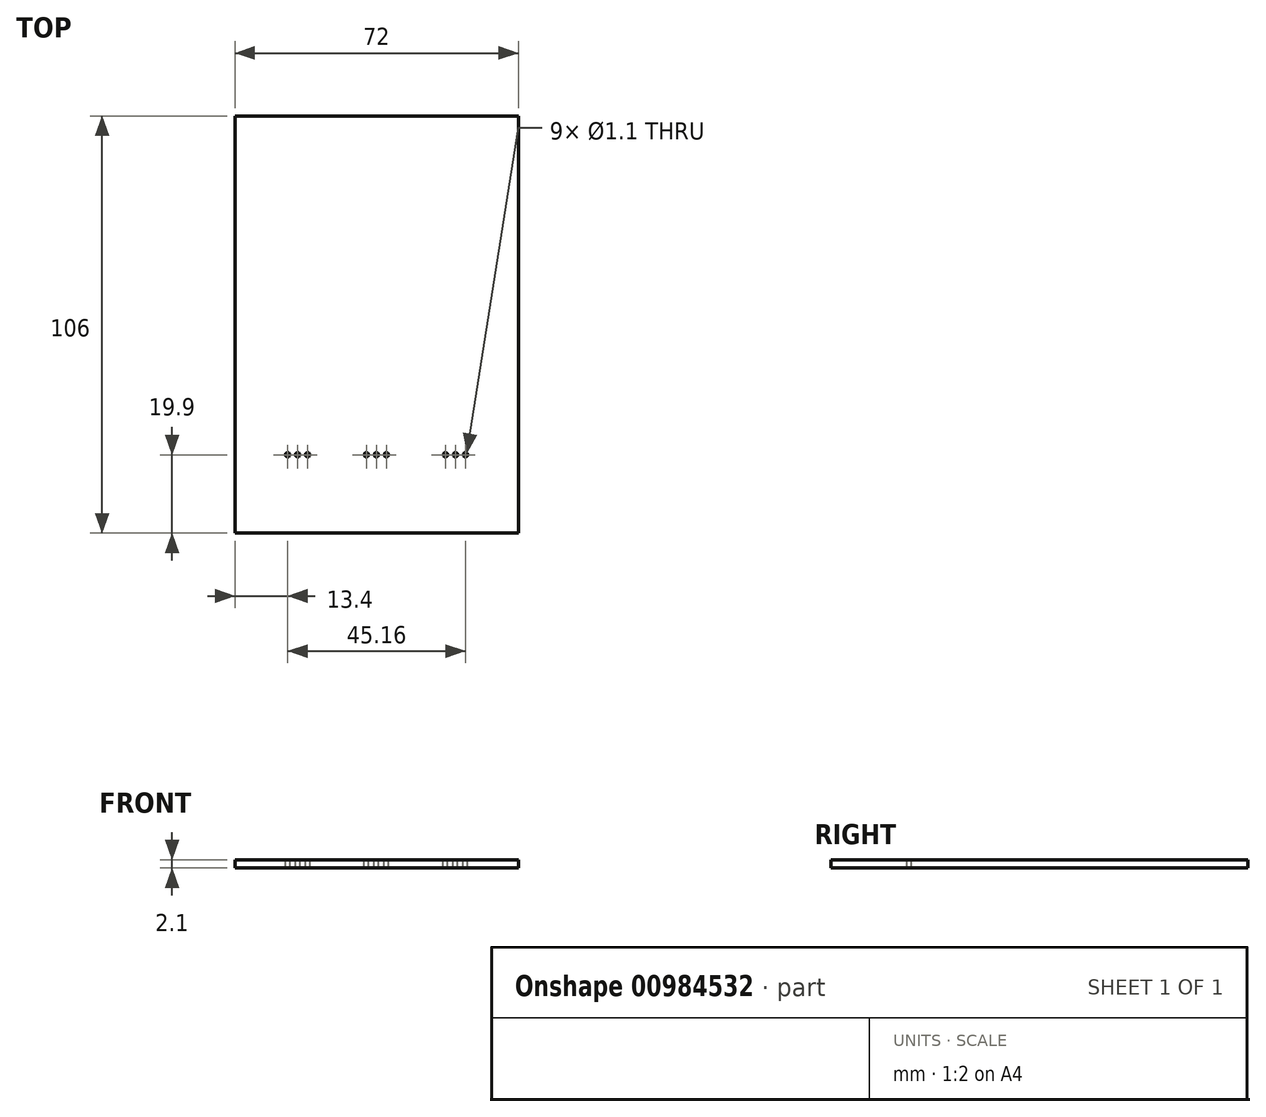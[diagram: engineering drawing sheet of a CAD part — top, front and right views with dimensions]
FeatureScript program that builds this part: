
annotation { "Feature Type Name" : "Feature", "Feature Type Description" : "" }
export const myFeature = defineFeature(function(context is Context, id is Id, definition is map)
    precondition{}
    {
        {
            var Q0;
            Q0=qCreatedBy(makeId("Top.planeOp"),FACE);
            var sketch = newSketch(context, id + "F0", { "sketchPlane" : qUnion([Q0])});
            skLineSegment(sketch, "E0.bottom", {"start": v(0, 0) * mm, "end": v(72, 0) * mm});
            skLineSegment(sketch, "E0.top", {"start": v(0, 106) * mm, "end": v(72, 106) * mm});
            skLineSegment(sketch, "E0.left", {"start": v(0, 0) * mm, "end": v(0, 106) * mm});
            skLineSegment(sketch, "E0.right", {"start": v(72, 0) * mm, "end": v(72, 106) * mm});
            skSolve(sketch);
        }
        {
            var Q0;
            Q0=makeQuery(id+"F0.imprint","IMPRINT",FACE,{"disambiguationData":[TD([[makeQuery(id+"F0.imprint","IMPRINT",EDGE,{"derivedFrom":sQuery(id+"F0.wireOp",EDGE,"E0.bottom")}),1.0]])]});
            extrude(context, id + "F1", {"entities" : qUnion([Q0]), "depth" : 2.1 * mm, "offsetDistance" : 25 * mm});
        }
        {
            var Q0;
            Q0=makeQuery(id+"F1.opExtrude","CAP_FACE",FACE,{"disambiguationData":[OSD([sQuery(id+"F0.wireOp",EDGE,"E0.bottom"),sQuery(id+"F0.wireOp",EDGE,"E0.top"),sQuery(id+"F0.wireOp",EDGE,"E0.left"),sQuery(id+"F0.wireOp",EDGE,"E0.right")])],"isStart":false});
            var sketch = newSketch(context, id + "F2", { "sketchPlane" : qUnion([Q0])});
            skPoint(sketch, "E1", {"position": v(13.4, 19.9) * mm});
            skPoint(sketch, "E2", {"position": v(15.94, 19.9) * mm});
            skPoint(sketch, "E3", {"position": v(18.48, 19.9) * mm});
            skPoint(sketch, "E4", {"position": v(33.4, 19.9) * mm});
            skPoint(sketch, "E5", {"position": v(35.94, 19.9) * mm});
            skPoint(sketch, "E6", {"position": v(38.48, 19.9) * mm});
            skPoint(sketch, "E7", {"position": v(53.48, 19.9) * mm});
            skPoint(sketch, "E8", {"position": v(56.02, 19.9) * mm});
            skPoint(sketch, "E9", {"position": v(58.56, 19.9) * mm});
            skSolve(sketch);
        }
        {
            var Q0;
            Q0=sQuery(id+"F2.wireOp",VERTEX,"E1");
            var Q1;
            Q1=sQuery(id+"F2.wireOp",VERTEX,"E2");
            var Q2;
            Q2=sQuery(id+"F2.wireOp",VERTEX,"E3");
            var Q3;
            Q3=sQuery(id+"F2.wireOp",VERTEX,"E4");
            var Q4;
            Q4=sQuery(id+"F2.wireOp",VERTEX,"E5");
            var Q5;
            Q5=sQuery(id+"F2.wireOp",VERTEX,"E6");
            var Q6;
            Q6=sQuery(id+"F2.wireOp",VERTEX,"E7");
            var Q7;
            Q7=sQuery(id+"F2.wireOp",VERTEX,"E8");
            var Q8;
            Q8=sQuery(id+"F2.wireOp",VERTEX,"E9");
            var Q9;
            Q9=makeQuery(id+"F1.opExtrude","SWEPT_BODY",BODY,{"disambiguationData":[OSD([sQuery(id+"F0.wireOp",EDGE,"E0.bottom"),sQuery(id+"F0.wireOp",EDGE,"E0.top"),sQuery(id+"F0.wireOp",EDGE,"E0.left"),sQuery(id+"F0.wireOp",EDGE,"E0.right")])]});
            hole(context, id + "F3", {"style" : HoleStyle.SIMPLE, "endStyle" : HoleEndStyle.THROUGH, "standardTappedOrClearance" : lookupTablePath({ "fit" : "Close", "standard" : "ISO", "size" : "M1", "type" : "Clearance" }), "standardBlindInLast" : lookupTablePath({ "fit" : "Close", "standard" : "ISO", "engagement" : "75%", "pitch" : "0.2 mm", "size" : "M1", "type" : "Clearance & tapped" }), "holeDiameter" : 1.1 * mm, "majorDiameter" : 5 * mm, "tappedDepth" : 12 * mm, "tapClearance" : 3, "locations" : qUnion([Q0, Q1, Q2, Q3, Q4, Q5, Q6, Q7, Q8]), "scope" : qUnion([Q9])});
        }
    });
